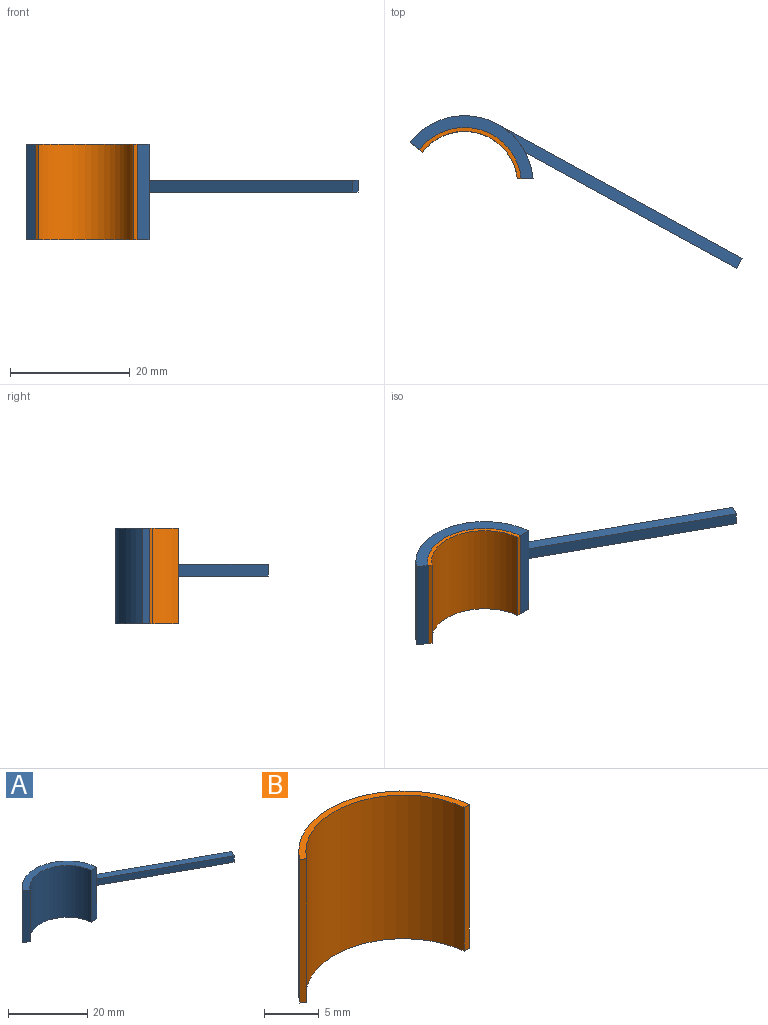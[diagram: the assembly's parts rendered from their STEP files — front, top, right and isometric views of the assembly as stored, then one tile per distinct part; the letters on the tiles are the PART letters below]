
ASSEMBLY  parts=2 mates=1
PART A: 11 faces, bbox 55.5x25.5x16 mm
  f0: cylinder r=11.5mm len=20.58mm, axis (0,0,-1), area 428.1mm2, adj f1,f3,f4,f5,f6,f8,f9,f10
  f1: plane 16x1.57mm, normal (-0.61,-0.79,0), area 31.6mm2, adj f0,f2,f4,f5
  f2: cylinder r=9.53mm len=17.03mm, axis (0,0,-1), area 363mm2, adj f1,f3,f4,f5
  f3: plane 16x1.98mm, normal (0,-1,0), area 31.7mm2, adj f0,f2,f4,f5
  f4: plane 20.58x10.5mm, normal (0,0,1), area 49.7mm2, adj f0,f1,f2,f3
  f5: plane 20.58x10.5mm, normal (0,0,-1), area 49.7mm2, adj f0,f1,f2,f3
  f6: plane 35.31x19.36mm, normal (-0.48,-0.88,0), area 80.5mm2, adj f0,f7,f9,f10
  f7: plane 2x1.69mm, normal (0.88,-0.48,0), area 3.8mm2, adj f6,f8,f9,f10
  f8: plane 40.9x22.42mm, normal (0.48,0.88,0), area 93.3mm2, adj f0,f7,f9,f10
  f9: plane 40.9x24.1mm, normal (0,0,1), area 81.4mm2, adj f0,f6,f7,f8
  f10: plane 40.9x24.1mm, normal (0,0,-1), area 81.4mm2, adj f0,f6,f7,f8
PART B: 6 faces, bbox 17x8.5x16 mm
  f0: cylinder r=8.87mm len=16mm, axis (0,0,-1), area 337.1mm2, adj f1,f3,f4,f5
  f1: plane 16x0.66mm, normal (0,-1,0), area 10.5mm2, adj f0,f2,f4,f5
  f2: cylinder r=9.53mm len=17.03mm, axis (0,0,-1), area 363mm2, adj f1,f3,f4,f5
  f3: plane 16x0.52mm, normal (-0.61,-0.79,0), area 10.4mm2, adj f0,f2,f4,f5
  f4: plane 17.03x8.53mm, normal (0,0,1), area 14.3mm2, adj f0,f1,f2,f3
  f5: plane 17.03x8.53mm, normal (0,0,-1), area 14.3mm2, adj f0,f1,f2,f3
PLACE A t=(-7.68,-16.24,-10.64)mm
PLACE B t=(-7.68,-16.24,-10.64)mm
MATE fastened A.f0 <-> B.f0  axis (0,0,-1) through (-7.68,-16.24,-10.64)mm
